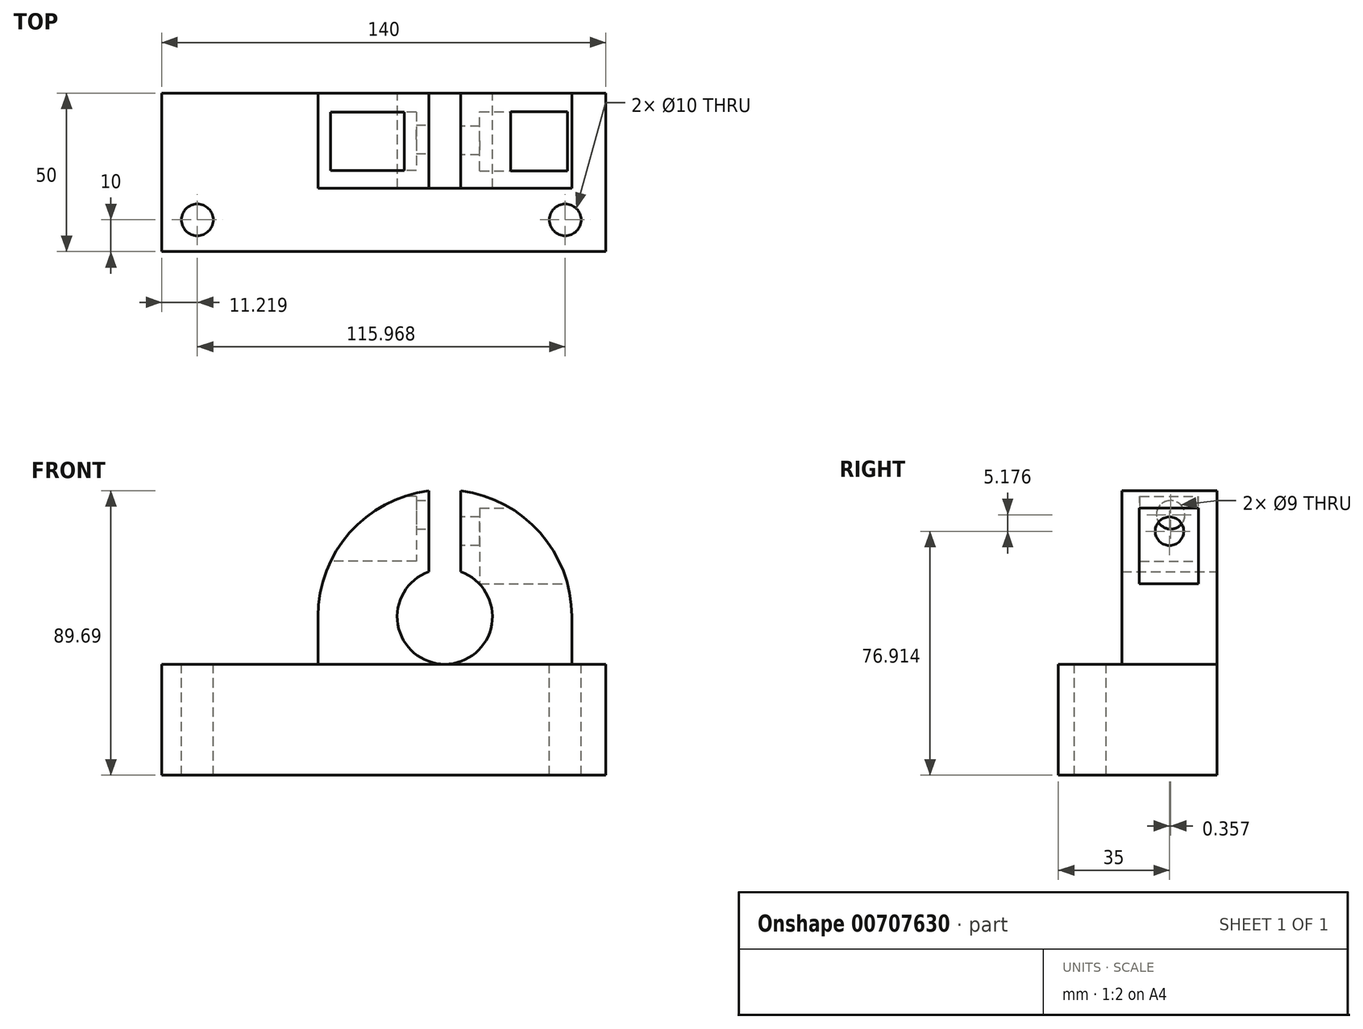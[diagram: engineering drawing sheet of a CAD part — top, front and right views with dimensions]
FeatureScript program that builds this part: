
annotation { "Feature Type Name" : "Feature", "Feature Type Description" : "" }
export const myFeature = defineFeature(function(context is Context, id is Id, definition is map)
    precondition{}
    {
        {
            var Q0;
            Q0=qCreatedBy(makeId("Front.planeOp"),FACE);
            var sketch = newSketch(context, id + "F0", { "sketchPlane" : qUnion([Q0])});
            skCircle(sketch, "E0", {"center": v(0, 0) * mm, "radius": 15 * mm});
            skCircle(sketch, "E1", {"center": v(0, 0) * mm, "radius": 40 * mm});
            skLineSegment(sketch, "E2", {"start": v(0, -15) * mm, "end": v(50.77, -15) * mm});
            skLineSegment(sketch, "E3", {"start": v(50.77, -15) * mm, "end": v(50.77, -50) * mm});
            skLineSegment(sketch, "E4", {"start": v(50.77, -50) * mm, "end": v(-89.23, -50) * mm});
            skLineSegment(sketch, "E5", {"start": v(-89.23, -50) * mm, "end": v(-89.23, -15) * mm});
            skLineSegment(sketch, "E6", {"start": v(-89.23, -15) * mm, "end": v(0, -15) * mm});
            skLineSegment(sketch, "E7", {"start": v(-5, 14.14) * mm, "end": v(-5, 39.69) * mm});
            skLineSegment(sketch, "E8.MirrorCS", {"start": v(5, 14.14) * mm, "end": v(5, 39.69) * mm});
            skLineSegment(sketch, "E9", {"start": v(40, 0) * mm, "end": v(40, -15) * mm});
            skLineSegment(sketch, "E10", {"start": v(-40, 0) * mm, "end": v(-40, -15) * mm});
            skSolve(sketch);
        }
        {
            var Q0;
            {var subQ0=sQuery(id+"F0.wireOp",EDGE,"E3");Q0=makeQuery(id+"F0.imprint","IMPRINT",FACE,{"disambiguationData":[TD([[makeQuery(id+"F0.imprint","IMPRINT",EDGE,{"derivedFrom":subQ0}),-1.0]])]});}
            var Q1;
            {var subQ0=sQuery(id+"F0.wireOp",EDGE,"E6");var subQ1=sQuery(id+"F0.wireOp",EDGE,"E1");var subQ2=makeQuery(id+"F0.imprint","INTERSECT",VERTEX,{"derivedFrom":[subQ1,subQ0]});Q1=makeQuery(id+"F0.imprint","IMPRINT",FACE,{"disambiguationData":[TD([[makeQuery(id+"F0.imprint","IMPRINT",EDGE,{"disambiguationData":[TD([[subQ2,-1.0]])],"derivedFrom":subQ1}),1.0]])]});}
            extrude(context, id + "F1", {"entities" : qUnion([Q0, Q1]), "depth" : 50 * mm, "offsetDistance" : 25 * mm});
        }
        {
            var Q0;
            {var subQ0=sQuery(id+"F0.wireOp",EDGE,"E3");Q0=makeQuery(id+"F0.imprint","IMPRINT",FACE,{"disambiguationData":[TD([[makeQuery(id+"F0.imprint","IMPRINT",EDGE,{"derivedFrom":subQ0}),-1.0]])]});}
            var Q1;
            {var subQ3=sQuery(id+"F0.wireOp",EDGE,"E7");Q1=makeQuery(id+"F0.imprint","IMPRINT",FACE,{"disambiguationData":[TD([[makeQuery(id+"F0.imprint","IMPRINT",EDGE,{"derivedFrom":subQ3}),1.0]])]});}
            var Q2;
            {var subQ3=sQuery(id+"F0.wireOp",EDGE,"E8.MirrorCS");Q2=makeQuery(id+"F0.imprint","IMPRINT",FACE,{"disambiguationData":[TD([[makeQuery(id+"F0.imprint","IMPRINT",EDGE,{"derivedFrom":subQ3}),-1.0]])]});}
            var Q3;
            {var subQ0=sQuery(id+"F0.wireOp",EDGE,"E6");var subQ1=sQuery(id+"F0.wireOp",EDGE,"E1");var subQ2=makeQuery(id+"F0.imprint","INTERSECT",VERTEX,{"derivedFrom":[subQ1,subQ0]});Q3=makeQuery(id+"F0.imprint","IMPRINT",FACE,{"disambiguationData":[TD([[makeQuery(id+"F0.imprint","IMPRINT",EDGE,{"disambiguationData":[TD([[subQ2,-1.0]])],"derivedFrom":subQ1}),1.0]])]});}
            var Q4;
            {var subQ0=sQuery(id+"F0.wireOp",EDGE,"E10");Q4=makeQuery(id+"F0.imprint","IMPRINT",FACE,{"disambiguationData":[TD([[makeQuery(id+"F0.imprint","IMPRINT",EDGE,{"derivedFrom":subQ0}),1.0]])]});}
            var Q5;
            {var subQ0=sQuery(id+"F0.wireOp",EDGE,"E9");Q5=makeQuery(id+"F0.imprint","IMPRINT",FACE,{"disambiguationData":[TD([[makeQuery(id+"F0.imprint","IMPRINT",EDGE,{"derivedFrom":subQ0}),-1.0]])]});}
            extrude(context, id + "F2", {"entities" : qUnion([Q0, Q1, Q2, Q3, Q4, Q5]), "operationType" : NewBodyOperationType.ADD, "depth" : 30 * mm, "offsetDistance" : 25 * mm});
        }
        {
            var Q0;
            Q0=makeQuery(id+"F2.opExtrude","SWEPT_FACE",FACE,{"disambiguationData":[OSD([sQuery(id+"F0.wireOp",EDGE,"E8.MirrorCS")])]});
            var sketch = newSketch(context, id + "F3", { "sketchPlane" : qUnion([Q0])});
            skCircle(sketch, "E11", {"center": v(15, 26.91) * mm, "radius": 4.5 * mm});
            skPoint(sketch, "E11.centerSnap0", {"position": v(15, 39.69) * mm});
            skPoint(sketch, "E11.centerSnap1", {"position": v(0, 26.91) * mm});
            skSolve(sketch);
        }
        {
            var Q0;
            Q0 = qSketchRegion(id + "F3", true);
            extrude(context, id + "F4", {"entities" : qUnion([Q0]), "operationType" : NewBodyOperationType.REMOVE, "endBound" : BoundingType.THROUGH_ALL, "oppositeDirection" : true, "depth" : 25 * mm, "offsetDistance" : 25 * mm});
        }
        {
            var Q0;
            Q0=makeQuery(id+"F2.opExtrude","SWEPT_FACE",FACE,{"disambiguationData":[OSD([sQuery(id+"F0.wireOp",EDGE,"E7")])]});
            var sketch = newSketch(context, id + "F5", { "sketchPlane" : qUnion([Q0])});
            skCircle(sketch, "E12", {"center": v(-14.64, 32.1) * mm, "radius": 4.5 * mm});
            skSolve(sketch);
        }
        {
            var Q0;
            Q0 = qSketchRegion(id + "F5", true);
            extrude(context, id + "F6", {"entities" : qUnion([Q0]), "operationType" : NewBodyOperationType.REMOVE, "endBound" : BoundingType.THROUGH_ALL, "oppositeDirection" : true, "depth" : 25 * mm, "offsetDistance" : 25 * mm});
        }
        {
            var Q0;
            Q0=makeQuery(id+"F1.opExtrude","SWEPT_FACE",FACE,{"disambiguationData":[OSD([sQuery(id+"F0.wireOp",EDGE,"E2"),sQuery(id+"F0.wireOp",EDGE,"E6")])]});
            var sketch = newSketch(context, id + "F7", { "sketchPlane" : qUnion([Q0])});
            skCircle(sketch, "E13", {"center": v(-78.01, -40) * mm, "radius": 5 * mm});
            skCircle(sketch, "E14", {"center": v(37.96, -40) * mm, "radius": 5 * mm});
            skSolve(sketch);
        }
        {
            var Q0;
            Q0 = qSketchRegion(id + "F7", true);
            extrude(context, id + "F8", {"entities" : qUnion([Q0]), "operationType" : NewBodyOperationType.REMOVE, "oppositeDirection" : true, "depth" : 57 * mm, "offsetDistance" : 25 * mm});
        }
        {
            var Q0;
            Q0=makeQuery(id+"F2.opExtrude","SWEPT_FACE",FACE,{"disambiguationData":[OSD([sQuery(id+"F0.wireOp",EDGE,"E10")])]});
            var sketch = newSketch(context, id + "F9", { "sketchPlane" : qUnion([Q0])});
            skLineSegment(sketch, "E15.bottom", {"start": v(6, 37.89) * mm, "end": v(24.4, 37.89) * mm});
            skLineSegment(sketch, "E15.top", {"start": v(6, 17.5) * mm, "end": v(24.4, 17.5) * mm});
            skLineSegment(sketch, "E15.left", {"start": v(6, 37.89) * mm, "end": v(6, 17.5) * mm});
            skLineSegment(sketch, "E15.right", {"start": v(24.4, 37.89) * mm, "end": v(24.4, 17.5) * mm});
            skPoint(sketch, "E15.middle", {"position": v(15.2, 27.69) * mm});
            skSolve(sketch);
        }
        {
            var Q0;
            Q0 = qSketchRegion(id + "F9", true);
            extrude(context, id + "F10", {"entities" : qUnion([Q0]), "operationType" : NewBodyOperationType.REMOVE, "oppositeDirection" : true, "depth" : 31 * mm, "offsetDistance" : 25 * mm});
        }
        {
            var Q0;
            Q0=makeQuery(id+"F2.opExtrude","SWEPT_FACE",FACE,{"disambiguationData":[OSD([sQuery(id+"F0.wireOp",EDGE,"E9")])]});
            var sketch = newSketch(context, id + "F11", { "sketchPlane" : qUnion([Q0])});
            skLineSegment(sketch, "E16.bottom", {"start": v(-24.5, 34.18) * mm, "end": v(-5.9, 34.18) * mm});
            skLineSegment(sketch, "E16.top", {"start": v(-24.5, 10.3) * mm, "end": v(-5.9, 10.3) * mm});
            skLineSegment(sketch, "E16.left", {"start": v(-24.5, 34.18) * mm, "end": v(-24.5, 10.3) * mm});
            skLineSegment(sketch, "E16.right", {"start": v(-5.9, 34.18) * mm, "end": v(-5.9, 10.3) * mm});
            skPoint(sketch, "E16.middle", {"position": v(-15.2, 22.24) * mm});
            skSolve(sketch);
        }
        {
            var Q0;
            Q0 = qSketchRegion(id + "F11", true);
            extrude(context, id + "F12", {"entities" : qUnion([Q0]), "operationType" : NewBodyOperationType.REMOVE, "oppositeDirection" : true, "depth" : 29 * mm, "offsetDistance" : 25 * mm});
        }
    });
